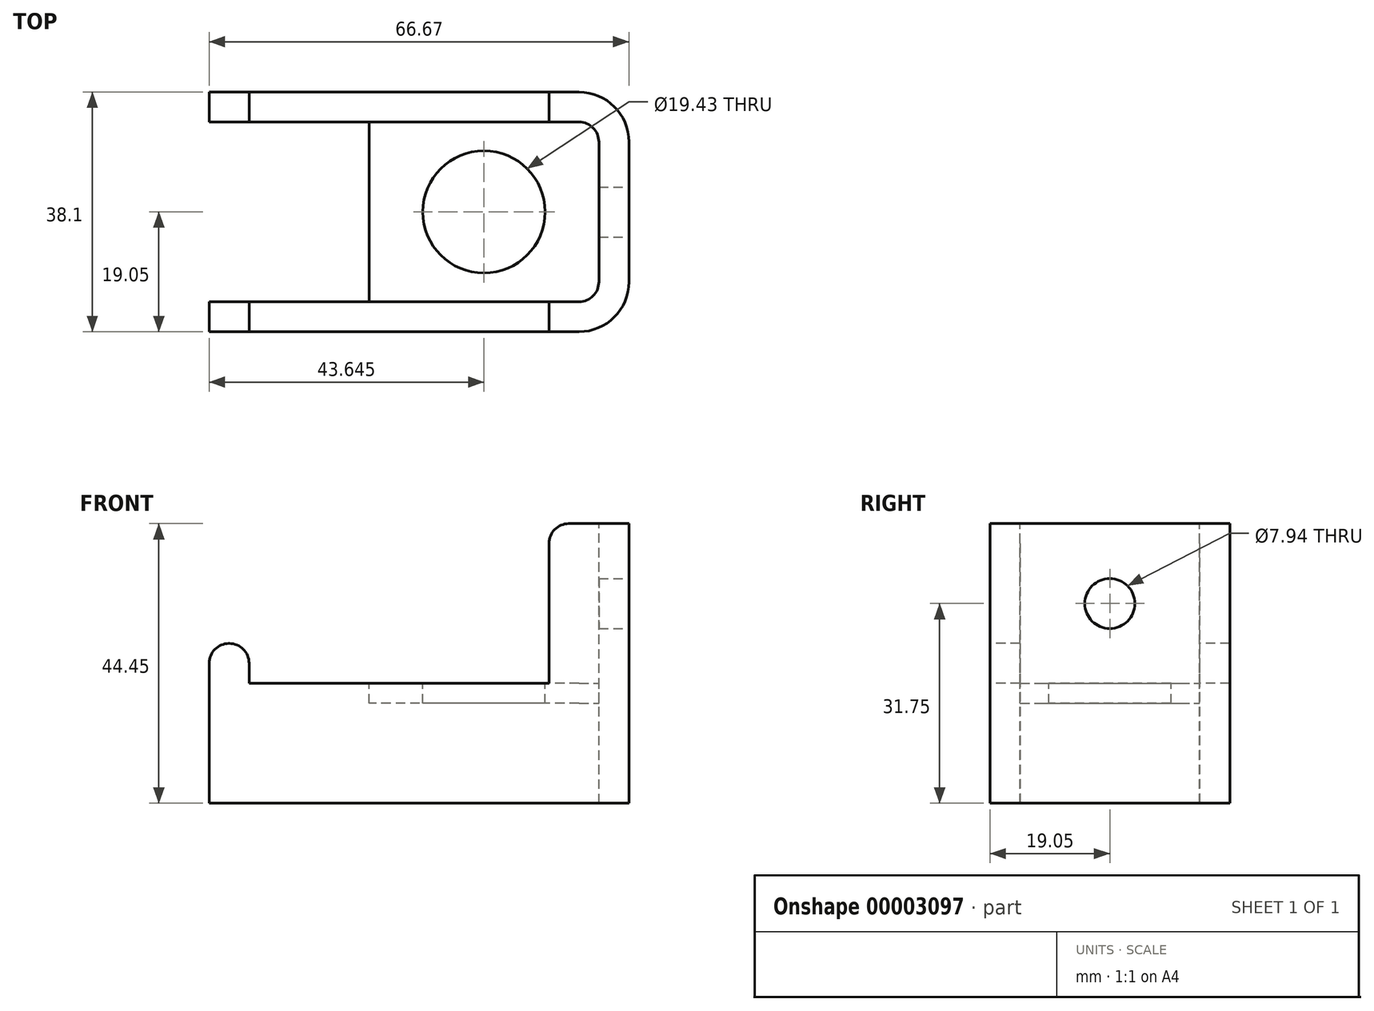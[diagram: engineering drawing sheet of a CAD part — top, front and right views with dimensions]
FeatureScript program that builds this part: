
annotation { "Feature Type Name" : "Feature", "Feature Type Description" : "" }
export const myFeature = defineFeature(function(context is Context, id is Id, definition is map)
    precondition{}
    {
        {
            var Q0;
            Q0=qCreatedBy(makeId("Front.planeOp"),FACE);
            var sketch = newSketch(context, id + "F0", { "sketchPlane" : qUnion([Q0])});
            skLineSegment(sketch, "E0", {"start": v(0, 0) * mm, "end": v(0, 44.45) * mm});
            skLineSegment(sketch, "E1", {"start": v(0, 44.45) * mm, "end": v(-9.55, 44.45) * mm});
            skLineSegment(sketch, "E2", {"start": v(-12.7, 41.3) * mm, "end": v(-12.7, 19.05) * mm});
            skLineSegment(sketch, "E3", {"start": v(-12.7, 19.05) * mm, "end": v(-60.33, 19.05) * mm});
            skLineSegment(sketch, "E4", {"start": v(-60.33, 19.05) * mm, "end": v(-60.33, 22.25) * mm});
            skLineSegment(sketch, "E5", {"start": v(-63.47, 25.4) * mm, "end": v(-63.53, 25.4) * mm});
            skLineSegment(sketch, "E6", {"start": v(-66.68, 22.25) * mm, "end": v(-66.68, 0) * mm});
            skLineSegment(sketch, "E7", {"start": v(-66.67, 0) * mm, "end": v(0, 0) * mm});
            skPoint(sketch, "E8.visualSharp", {"position": v(-66.68, 25.4) * mm});
            skArc(sketch, "E8.filletArc", {"start": v(-63.53, 25.4) * mm, "mid": v(-65.75, 24.48) * mm, "end": v(-66.68, 22.25) * mm});
            skPoint(sketch, "E9.visualSharp", {"position": v(-60.33, 25.4) * mm});
            skArc(sketch, "E9.filletArc", {"start": v(-60.33, 22.25) * mm, "mid": v(-61.25, 24.48) * mm, "end": v(-63.47, 25.4) * mm});
            skPoint(sketch, "E10.visualSharp", {"position": v(-12.7, 44.45) * mm});
            skArc(sketch, "E10.filletArc", {"start": v(-9.55, 44.45) * mm, "mid": v(-11.78, 43.53) * mm, "end": v(-12.7, 41.3) * mm});
            skSolve(sketch);
        }
        {
            var Q0;
            Q0 = qSketchRegion(id + "F0", true);
            extrude(context, id + "F1", {"entities" : qUnion([Q0]), "oppositeDirection" : true, "depth" : 38.1 * mm});
        }
        {
            var Q0;
            Q0=makeQuery(id+"F1.opExtrude","SWEPT_FACE",FACE,{"disambiguationData":[OSD([sQuery(id+"F0.wireOp",EDGE,"E1")])]});
            var sketch = newSketch(context, id + "F2", { "sketchPlane" : qUnion([Q0])});
            skLineSegment(sketch, "E11.bottom", {"start": v(-4.78, 33.32) * mm, "end": v(-68.57, 33.32) * mm});
            skLineSegment(sketch, "E11.top", {"start": v(-4.78, 4.78) * mm, "end": v(-68.57, 4.78) * mm});
            skLineSegment(sketch, "E11.left", {"start": v(-4.78, 33.32) * mm, "end": v(-4.78, 4.78) * mm});
            skLineSegment(sketch, "E11.right", {"start": v(-68.57, 33.32) * mm, "end": v(-68.57, 4.78) * mm});
            skSolve(sketch);
        }
        {
            var Q0;
            Q0 = qSketchRegion(id + "F2", true);
            extrude(context, id + "F3", {"entities" : qUnion([Q0]), "operationType" : NewBodyOperationType.REMOVE, "endBound" : BoundingType.THROUGH_ALL, "oppositeDirection" : true, "depth" : 25.4 * mm});
        }
        {
            var Q0;
            {var subQ0=sQuery(id+"F0.wireOp",EDGE,"E3");Q0=makeQuery(id+"F3.boolean.opBoolean","SPLIT",FACE,{"disambiguationData":[TD([makeQuery(id+"F3.opExtrude","SWEPT_FACE",FACE,{"disambiguationData":[OSD([sQuery(id+"F2.wireOp",EDGE,"E11.top")])]})])],"derivedFrom":makeQuery(id+"F1.opExtrude","SWEPT_FACE",FACE,{"disambiguationData":[OSD([subQ0])]})});}
            var sketch = newSketch(context, id + "F4", { "sketchPlane" : qUnion([Q0])});
            skLineSegment(sketch, "E12.bottom", {"start": v(-7.92, 4.78) * mm, "end": v(-41.28, 4.78) * mm});
            skLineSegment(sketch, "E12.top", {"start": v(-7.92, 33.32) * mm, "end": v(-41.28, 33.32) * mm});
            skLineSegment(sketch, "E12.left", {"start": v(-4.78, 7.92) * mm, "end": v(-4.78, 30.18) * mm});
            skLineSegment(sketch, "E12.right", {"start": v(-41.28, 4.78) * mm, "end": v(-41.28, 33.32) * mm});
            skCircle(sketch, "E13", {"center": v(-23.03, 19.05) * mm, "radius": 9.72 * mm});
            skPoint(sketch, "E14.visualSharp", {"position": v(-4.78, 33.32) * mm});
            skArc(sketch, "E14.filletArc", {"start": v(-4.78, 30.18) * mm, "mid": v(-5.7, 32.4) * mm, "end": v(-7.92, 33.32) * mm});
            skPoint(sketch, "E15.visualSharp", {"position": v(-4.78, 4.78) * mm});
            skArc(sketch, "E15.filletArc", {"start": v(-7.92, 4.78) * mm, "mid": v(-5.7, 5.7) * mm, "end": v(-4.78, 7.92) * mm});
            skSolve(sketch);
        }
        {
            var Q0;
            Q0=makeQuery(id+"F4.imprint","IMPRINT",FACE,{"disambiguationData":[TD([[makeQuery(id+"F4.imprint","IMPRINT",EDGE,{"derivedFrom":sQuery(id+"F4.wireOp",EDGE,"E12.top")}),1.0]])]});
            extrude(context, id + "F5", {"entities" : qUnion([Q0]), "oppositeDirection" : true, "depth" : 3.17 * mm});
        }
        {
            var Q0;
            Q0=makeQuery(id+"F1.opExtrude","SWEPT_FACE",FACE,{"disambiguationData":[OSD([sQuery(id+"F0.wireOp",EDGE,"E0")])]});
            var sketch = newSketch(context, id + "F6", { "sketchPlane" : qUnion([Q0])});
            skCircle(sketch, "E16", {"center": v(19.05, 31.75) * mm, "radius": 3.97 * mm});
            skSolve(sketch);
        }
        {
            var Q0;
            Q0 = qSketchRegion(id + "F6", true);
            extrude(context, id + "F7", {"entities" : qUnion([Q0]), "operationType" : NewBodyOperationType.REMOVE, "endBound" : BoundingType.THROUGH_ALL, "oppositeDirection" : true, "depth" : 25.4 * mm});
        }
        {
            var Q0;
            Q0=makeQuery(id+"F1.opExtrude","CAP_EDGE",EDGE,{"disambiguationData":[OSD([sQuery(id+"F0.wireOp",EDGE,"E0")])],"isStart":true});
            var Q1;
            Q1=makeQuery(id+"F1.opExtrude","CAP_EDGE",EDGE,{"disambiguationData":[OSD([sQuery(id+"F0.wireOp",EDGE,"E0")])],"isStart":false});
            fillet(context, id + "F8", {"entities" : qUnion([Q0, Q1]), "radius" : 7.92 * mm, "tangentPropagation" : true, "allowEdgeOverflow" : false});
        }
        {
            var Q0;
            Q0=makeQuery(id+"F3.boolean.opBoolean","COPY",EDGE,{"derivedFrom":makeQuery(id+"F3.opExtrude","SWEPT_EDGE",EDGE,{"disambiguationData":[OSD([sQuery(id+"F2.wireOp",EDGE,"E11.top"),sQuery(id+"F2.wireOp",EDGE,"E11.left")])]})});
            var Q1;
            Q1=makeQuery(id+"F3.boolean.opBoolean","COPY",EDGE,{"derivedFrom":makeQuery(id+"F3.opExtrude","SWEPT_EDGE",EDGE,{"disambiguationData":[OSD([sQuery(id+"F2.wireOp",EDGE,"E11.bottom"),sQuery(id+"F2.wireOp",EDGE,"E11.left")])]})});
            fillet(context, id + "F9", {"entities" : qUnion([Q0, Q1]), "radius" : 3.15 * mm, "tangentPropagation" : true, "allowEdgeOverflow" : false});
        }
    });
